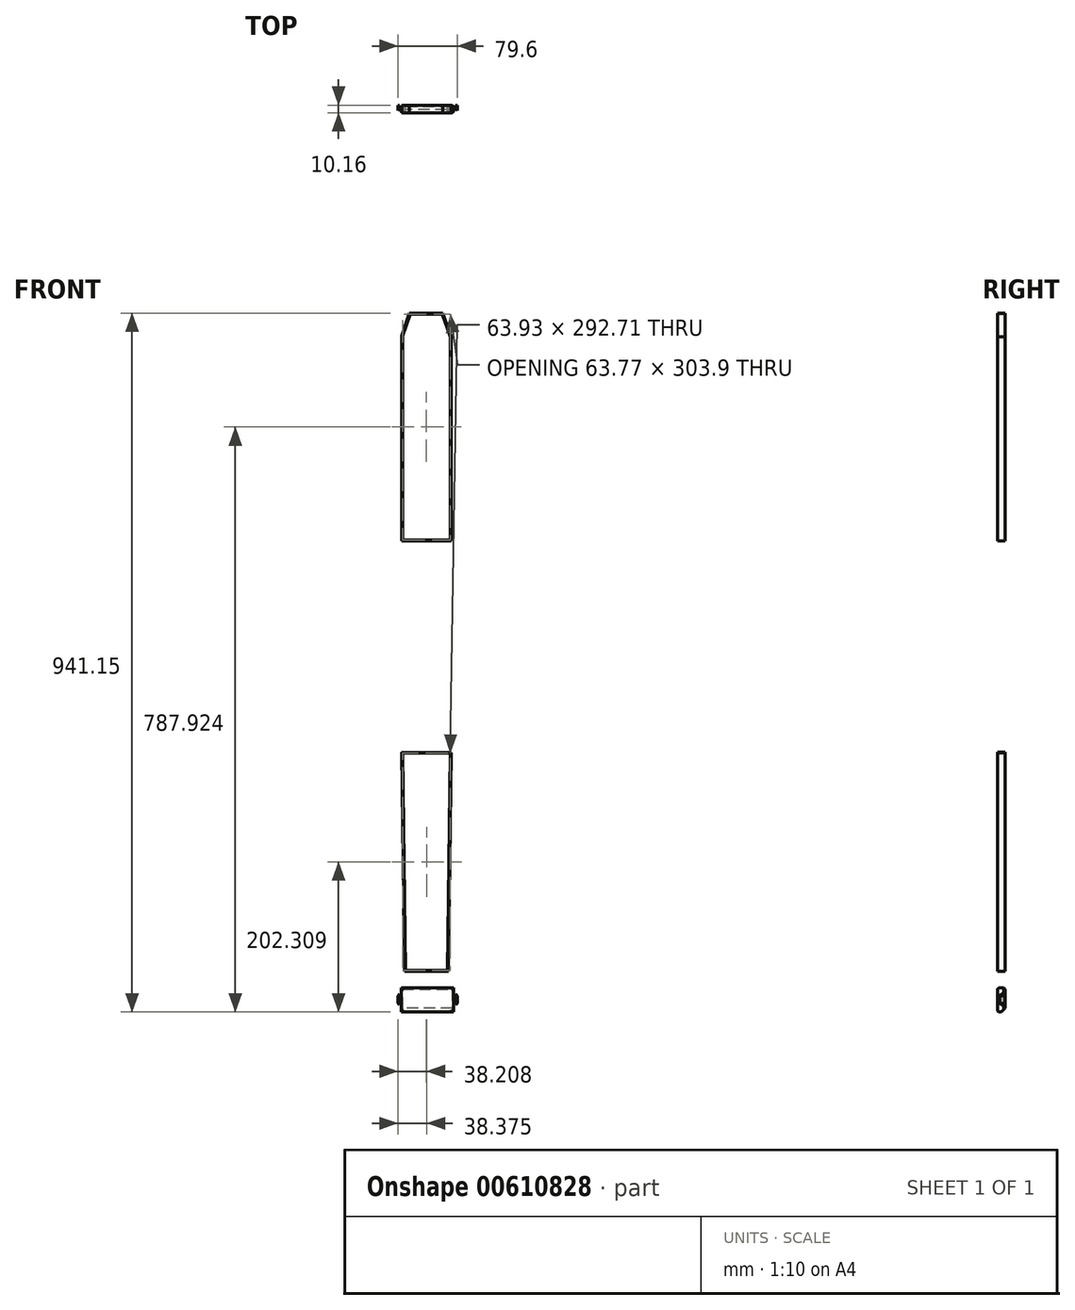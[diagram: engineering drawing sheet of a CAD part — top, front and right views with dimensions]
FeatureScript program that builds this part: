
annotation { "Feature Type Name" : "Feature", "Feature Type Description" : "" }
export const myFeature = defineFeature(function(context is Context, id is Id, definition is map)
    precondition{}
    {
        {
            var Q0;
            Q0=qCreatedBy(makeId("Front.planeOp"),FACE);
            cPlane(context, id + "F0", {"entities" : qUnion([Q0]), "cplaneType" : CPlaneType.OFFSET, "offset" : 17.78 * mm, "oppositeDirection" : true, "width" : 152.4 * mm, "height" : 152.4 * mm});
        }
        {
            var Q0;
            Q0=qCreatedBy(id+"F0.planeOp",FACE);
            cPlane(context, id + "F1", {"entities" : qUnion([Q0]), "cplaneType" : CPlaneType.OFFSET, "offset" : 25.4 * mm, "oppositeDirection" : true, "width" : 152.4 * mm, "height" : 152.4 * mm});
        }
        {
            var Q0;
            Q0=qCreatedBy(id+"F1.planeOp",FACE);
            var sketch = newSketch(context, id + "F2", { "sketchPlane" : qUnion([Q0])});
            skPoint(sketch, "E0.end.orphan", {"position": v(33.41, 331.77) * mm});
            skPoint(sketch, "E1.end.orphan", {"position": v(-33.96, 331.77) * mm});
            skLineSegment(sketch, "E2.0", {"start": v(30.92, 135.47) * mm, "end": v(-35.38, 135.47) * mm});
            skLineSegment(sketch, "E2.1", {"start": v(30.92, 135.47) * mm, "end": v(30.92, 410.49) * mm});
            skLineSegment(sketch, "E2.2", {"start": v(-25.1, 441.92) * mm, "end": v(-35.38, 411.41) * mm});
            skLineSegment(sketch, "E2.3", {"start": v(-25.1, 441.92) * mm, "end": v(-0.05, 441.81) * mm});
            skLineSegment(sketch, "E2.4", {"start": v(-0.05, 441.81) * mm, "end": v(19.85, 441.73) * mm});
            skLineSegment(sketch, "E2.5", {"start": v(-35.38, 135.47) * mm, "end": v(-35.38, 411.41) * mm});
            skLineSegment(sketch, "E2.6", {"start": v(19.85, 441.73) * mm, "end": v(30.92, 410.49) * mm});
            skPoint(sketch, "E3.end.orphan", {"position": v(-41.73, 412.45) * mm});
            skPoint(sketch, "E4.end.orphan", {"position": v(42.35, 412.45) * mm});
            skPoint(sketch, "E5.start.orphan", {"position": v(0, 453.24) * mm});
            skLineSegment(sketch, "E6.0", {"start": v(29.65, 136.74) * mm, "end": v(-34.11, 136.74) * mm});
            skLineSegment(sketch, "E6.1", {"start": v(29.65, 136.74) * mm, "end": v(29.65, 410.27) * mm});
            skLineSegment(sketch, "E6.2", {"start": v(-24.19, 440.64) * mm, "end": v(-34.11, 411.2) * mm});
            skLineSegment(sketch, "E6.3", {"start": v(-24.19, 440.64) * mm, "end": v(-0.05, 440.54) * mm});
            skLineSegment(sketch, "E6.4", {"start": v(-0.05, 440.54) * mm, "end": v(18.95, 440.46) * mm});
            skLineSegment(sketch, "E6.5", {"start": v(-34.11, 136.74) * mm, "end": v(-34.11, 411.2) * mm});
            skLineSegment(sketch, "E6.6", {"start": v(18.95, 440.46) * mm, "end": v(29.65, 410.27) * mm});
            skSolve(sketch);
        }
        {
            var Q0;
            Q0=qSketchRegion(id+"F2",true);
            extrude(context, id + "F3", {"entities" : qUnion([Q0]), "depth" : 10.16 * mm, "offsetDistance" : 25.4 * mm});
        }
        {
            var Q0;
            Q0=qCreatedBy(id+"F1.planeOp",FACE);
            var sketch = newSketch(context, id + "F4", { "sketchPlane" : qUnion([Q0])});
            skPoint(sketch, "E7.0.start.orphan", {"position": v(-41.97, -112.7) * mm});
            skLineSegment(sketch, "E8.0", {"start": v(31.19, -150.15) * mm, "end": v(-35.32, -149.28) * mm});
            skLineSegment(sketch, "E9.0", {"start": v(-31.93, -444.54) * mm, "end": v(-35.32, -149.28) * mm});
            skLineSegment(sketch, "E9.1", {"start": v(0, -444.54) * mm, "end": v(-31.93, -444.54) * mm});
            skLineSegment(sketch, "E9.2", {"start": v(0, -444.54) * mm, "end": v(27.32, -444.54) * mm});
            skLineSegment(sketch, "E9.3", {"start": v(27.32, -444.54) * mm, "end": v(31.19, -150.15) * mm});
            skLineSegment(sketch, "E10.0", {"start": v(-30.68, -443.27) * mm, "end": v(-34.03, -150.57) * mm});
            skLineSegment(sketch, "E10.1", {"start": v(29.9, -151.4) * mm, "end": v(-34.03, -150.57) * mm});
            skLineSegment(sketch, "E10.2", {"start": v(0, -443.27) * mm, "end": v(-30.68, -443.27) * mm});
            skLineSegment(sketch, "E10.3", {"start": v(0, -443.27) * mm, "end": v(26.07, -443.27) * mm});
            skLineSegment(sketch, "E10.4", {"start": v(26.07, -443.27) * mm, "end": v(29.9, -151.4) * mm});
            skSolve(sketch);
        }
        {
            var Q0;
            Q0=qSketchRegion(id+"F4",true);
            extrude(context, id + "F5", {"entities" : qUnion([Q0]), "depth" : 10.16 * mm, "offsetDistance" : 25.4 * mm});
        }
        {
            var Q0;
            Q0 = qSketchRegion(id + "F2", true);
            extrude(context, id + "F6", {"entities" : qUnion([Q0]), "operationType" : NewBodyOperationType.ADD, "depth" : 3.05 * mm, "offsetDistance" : 25.4 * mm});
        }
        {
            var Q0;
            Q0=qCreatedBy(id+"F1.planeOp",FACE);
            var sketch = newSketch(context, id + "F7", { "sketchPlane" : qUnion([Q0])});
            skLineSegment(sketch, "E11", {"start": v(-36.3, -467.03) * mm, "end": v(34.3, -467.03) * mm});
            skLineSegment(sketch, "E12", {"start": v(34.3, -467.03) * mm, "end": v(34.3, -499.23) * mm});
            skLineSegment(sketch, "E13", {"start": v(34.3, -499.23) * mm, "end": v(-36.3, -499.23) * mm});
            skLineSegment(sketch, "E14", {"start": v(-36.3, -499.23) * mm, "end": v(-36.3, -467.03) * mm});
            skLineSegment(sketch, "E15", {"start": v(-38.57, -474.73) * mm, "end": v(-38.57, -489.78) * mm});
            skLineSegment(sketch, "E16", {"start": v(37, -489.78) * mm, "end": v(37, -474.73) * mm});
            skLineSegment(sketch, "E17", {"start": v(-40.44, -477.3) * mm, "end": v(-40.44, -487.52) * mm});
            skLineSegment(sketch, "E18", {"start": v(39.16, -487.52) * mm, "end": v(39.16, -477.3) * mm});
            skLineSegment(sketch, "E19", {"start": v(37, -474.73) * mm, "end": v(39.16, -477.3) * mm});
            skLineSegment(sketch, "E20", {"start": v(39.16, -487.52) * mm, "end": v(37, -489.78) * mm});
            skLineSegment(sketch, "E21", {"start": v(-38.57, -474.73) * mm, "end": v(-40.44, -477.3) * mm});
            skLineSegment(sketch, "E22", {"start": v(-40.44, -487.52) * mm, "end": v(-38.57, -489.78) * mm});
            skSolve(sketch);
        }
        {
            var Q0;
            Q0 = qSketchRegion(id + "F7", true);
            extrude(context, id + "F8", {"entities" : qUnion([Q0]), "depth" : 10.16 * mm, "offsetDistance" : 25.4 * mm});
        }
        {
            var Q0;
            Q0=makeQuery(id+"F8.opExtrude","CAP_EDGE",EDGE,{"disambiguationData":[OSD([sQuery(id+"F7.wireOp",EDGE,"E13")])],"isStart":true});
            chamfer(context, id + "F9", {"entities" : qUnion([Q0]), "width" : 5.08 * mm, "tangentPropagation" : true});
        }
        {
            var Q0;
            Q0=makeQuery(id+"F8.opExtrude","CAP_EDGE",EDGE,{"disambiguationData":[OSD([sQuery(id+"F7.wireOp",EDGE,"E12")])],"isStart":true});
            var Q1;
            Q1=makeQuery(id+"F8.opExtrude","CAP_EDGE",EDGE,{"disambiguationData":[OSD([sQuery(id+"F7.wireOp",EDGE,"E11")])],"isStart":true});
            var Q2;
            Q2=makeQuery(id+"F8.opExtrude","CAP_EDGE",EDGE,{"disambiguationData":[OSD([sQuery(id+"F7.wireOp",EDGE,"E14")])],"isStart":true});
            chamfer(context, id + "F10", {"entities" : qUnion([Q0, Q1, Q2]), "width" : 1.78 * mm, "tangentPropagation" : true});
        }
        {
            var Q0;
            Q0=makeQuery(id+"F8.opExtrude","CAP_FACE",FACE,{"disambiguationData":[OSD([sQuery(id+"F7.wireOp",EDGE,"E11"),sQuery(id+"F7.wireOp",EDGE,"E12"),sQuery(id+"F7.wireOp",EDGE,"E13"),sQuery(id+"F7.wireOp",EDGE,"E14")])],"isStart":false});
            fillet(context, id + "F11", {"entities" : qUnion([Q0]), "radius" : 2.54 * mm, "tangentPropagation" : true, "allowEdgeOverflow" : false});
        }
        {
            var Q0;
            Q0=makeQuery(id+"F8.opExtrude","CAP_EDGE",EDGE,{"disambiguationData":[OSD([sQuery(id+"F7.wireOp",EDGE,"E16")])],"isStart":false});
            var Q1;
            Q1=makeQuery(id+"F8.opExtrude","CAP_EDGE",EDGE,{"disambiguationData":[OSD([sQuery(id+"F7.wireOp",EDGE,"E15")])],"isStart":false});
            chamfer(context, id + "F12", {"entities" : qUnion([Q0, Q1]), "width" : 5.08 * mm, "tangentPropagation" : true});
        }
    });
